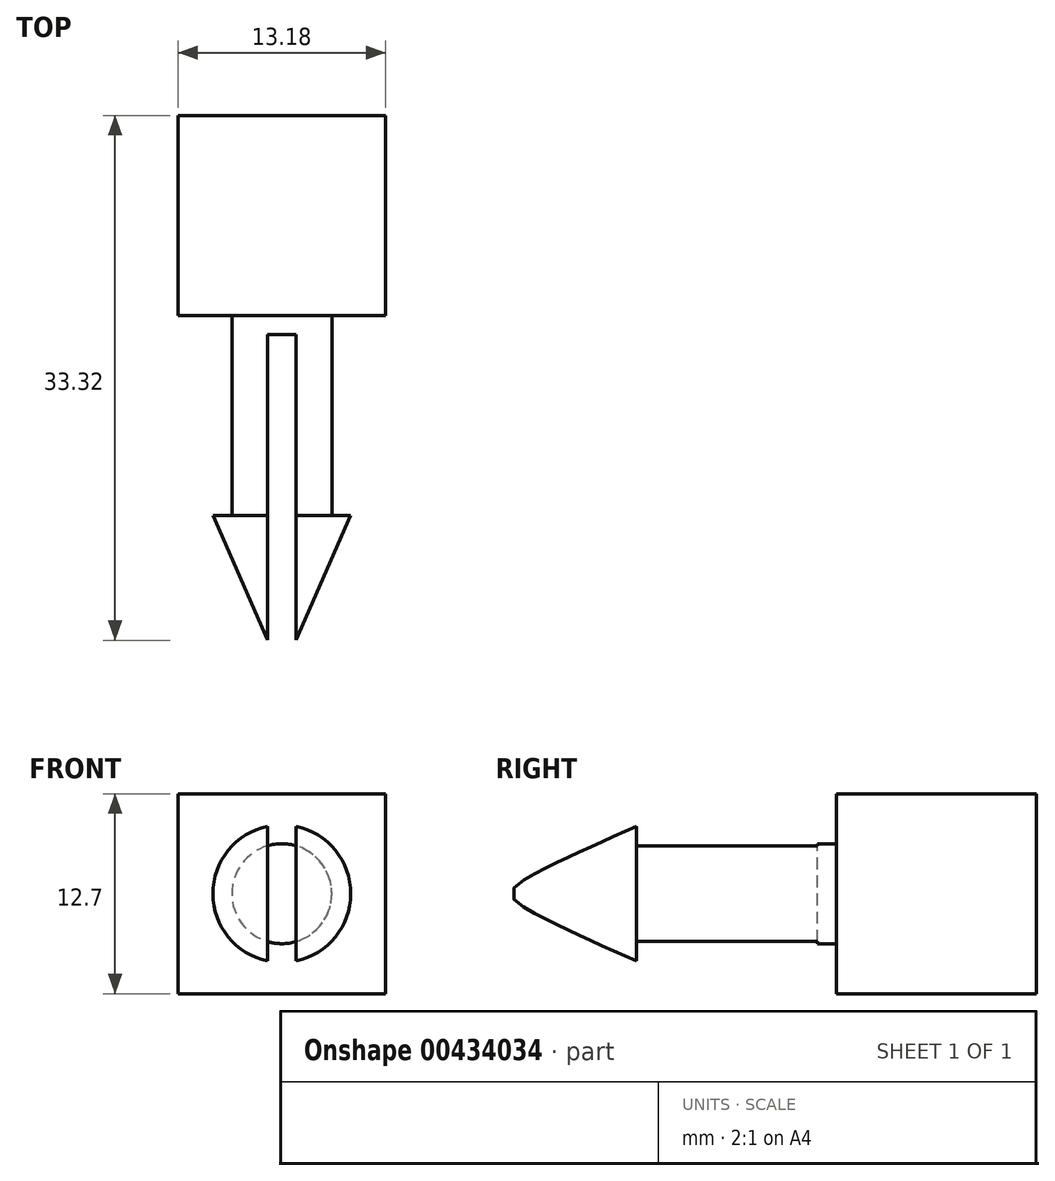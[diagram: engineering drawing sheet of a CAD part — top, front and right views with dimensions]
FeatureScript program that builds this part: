
annotation { "Feature Type Name" : "Feature", "Feature Type Description" : "" }
export const myFeature = defineFeature(function(context is Context, id is Id, definition is map)
    precondition{}
    {
        {
            var Q0;
            Q0=qCreatedBy(makeId("Front.planeOp"),FACE);
            var sketch = newSketch(context, id + "F0", { "sketchPlane" : qUnion([Q0])});
            skLineSegment(sketch, "E0.bottom", {"start": v(-6.59, 6.35) * mm, "end": v(6.59, 6.35) * mm});
            skLineSegment(sketch, "E0.top", {"start": v(-6.59, -6.35) * mm, "end": v(6.59, -6.35) * mm});
            skLineSegment(sketch, "E0.left", {"start": v(-6.59, 6.35) * mm, "end": v(-6.59, -6.35) * mm});
            skLineSegment(sketch, "E0.right", {"start": v(6.59, 6.35) * mm, "end": v(6.59, -6.35) * mm});
            skPoint(sketch, "E0.middle", {"position": v(0, 0) * mm});
            skSolve(sketch);
        }
        {
            var Q0;
            Q0 = qSketchRegion(id + "F0", true);
            extrude(context, id + "F1", {"entities" : qUnion([Q0]), "depth" : 12.7 * mm});
        }
        {
            var Q0;
            Q0=makeQuery(id+"F1.opExtrude","CAP_FACE",FACE,{"disambiguationData":[OSD([sQuery(id+"F0.wireOp",EDGE,"E0.bottom"),sQuery(id+"F0.wireOp",EDGE,"E0.top"),sQuery(id+"F0.wireOp",EDGE,"E0.left"),sQuery(id+"F0.wireOp",EDGE,"E0.right")])],"isStart":false});
            var sketch = newSketch(context, id + "F2", { "sketchPlane" : qUnion([Q0])});
            skCircle(sketch, "E1", {"center": v(0, 0) * mm, "radius": 3.17 * mm});
            skSolve(sketch);
        }
        {
            var Q0;
            Q0=makeQuery(id+"F2.imprint","IMPRINT",FACE,{"disambiguationData":[TD([[makeQuery(id+"F2.imprint","IMPRINT",EDGE,{"derivedFrom":sQuery(id+"F2.wireOp",EDGE,"E1")}),1.0]])]});
            var Q1;
            Q1 = qConstructionFilter(qBodyType(qCreatedBy(id + "F2" ,EDGE), BodyType.WIRE), ConstructionObject.NO);
            extrude(context, id + "F3", {"entities" : qUnion([Q0]), "operationType" : NewBodyOperationType.ADD, "surfaceEntities" : qUnion([Q1]), "depth" : 12.7 * mm});
        }
        {
            var Q0;
            Q0=qCreatedBy(makeId("Front.planeOp"),FACE);
            cPlane(context, id + "F4", {"entities" : qUnion([Q0]), "cplaneType" : CPlaneType.OFFSET, "offset" : 35.4 * mm, "width" : 150 * mm, "height" : 150 * mm});
        }
        {
            var Q0;
            Q0=qCreatedBy(id+"F4.planeOp",FACE);
            var sketch = newSketch(context, id + "F5", { "sketchPlane" : qUnion([Q0])});
            skPoint(sketch, "E2", {"position": v(0, 0) * mm});
            skSolve(sketch);
        }
        {
            var Q0;
            Q0=qCreatedBy(makeId("Front.planeOp"),FACE);
            cPlane(context, id + "F6", {"entities" : qUnion([Q0]), "cplaneType" : CPlaneType.OFFSET, "offset" : 25.4 * mm, "width" : 150 * mm, "height" : 150 * mm});
        }
        {
            var Q0;
            Q0=qCreatedBy(id+"F6.planeOp",FACE);
            var sketch = newSketch(context, id + "F7", { "sketchPlane" : qUnion([Q0])});
            skCircle(sketch, "E3", {"center": v(0, 0) * mm, "radius": 4.38 * mm});
            skSolve(sketch);
        }
        {
            var Q1;
            Q1 = qSketchRegion(id + "F7", true);
            var Q2;
            Q2=sQuery(id+"F5.wireOp",VERTEX,"E2");
            loft(context, id + "F8", {"operationType" : NewBodyOperationType.ADD, "sheetProfilesArray" : [{ "sheetProfileEntities" : qUnion([Q1]) }, { "sheetProfileEntities" : qUnion([Q2]) }]});
        }
        {
            var Q0;
            Q0=qCreatedBy(id+"F4.planeOp",FACE);
            var sketch = newSketch(context, id + "F9", { "sketchPlane" : qUnion([Q0])});
            skLineSegment(sketch, "E4.bottom", {"start": v(-0.91, -5.5) * mm, "end": v(0.91, -5.5) * mm});
            skLineSegment(sketch, "E4.top", {"start": v(-0.91, 5.5) * mm, "end": v(0.91, 5.5) * mm});
            skLineSegment(sketch, "E4.left", {"start": v(-0.91, -5.5) * mm, "end": v(-0.91, 5.5) * mm});
            skLineSegment(sketch, "E4.right", {"start": v(0.91, -5.5) * mm, "end": v(0.91, 5.5) * mm});
            skPoint(sketch, "E4.middle", {"position": v(0, 0) * mm});
            skSolve(sketch);
        }
        {
            var Q0;
            Q0 = qSketchRegion(id + "F9", true);
            extrude(context, id + "F10", {"entities" : qUnion([Q0]), "operationType" : NewBodyOperationType.REMOVE, "oppositeDirection" : true, "depth" : 21.5 * mm});
        }
    });
